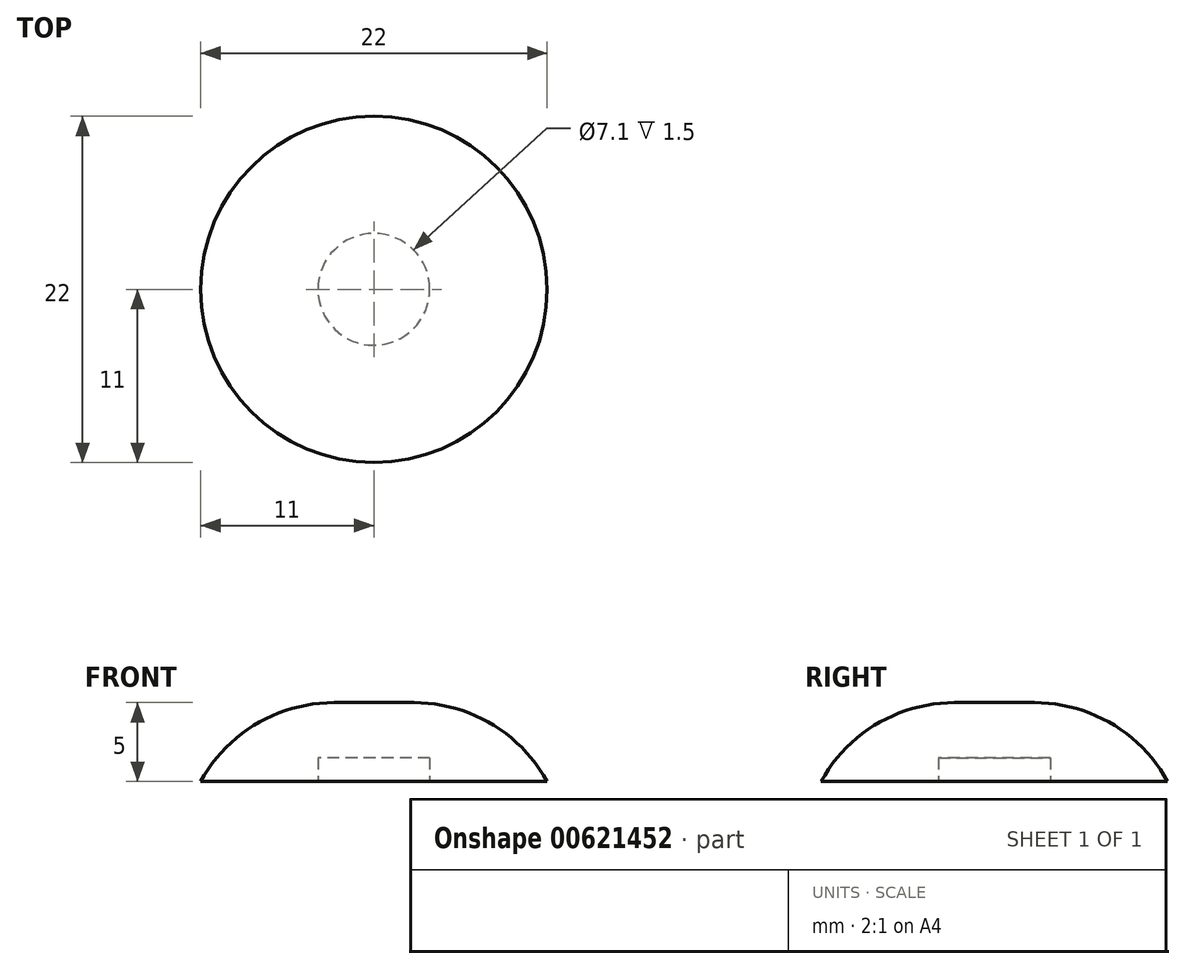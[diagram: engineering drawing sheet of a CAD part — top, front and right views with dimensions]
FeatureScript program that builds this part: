
annotation { "Feature Type Name" : "Feature", "Feature Type Description" : "" }
export const myFeature = defineFeature(function(context is Context, id is Id, definition is map)
    precondition{}
    {
        {
            var Q0;
            Q0=qCreatedBy(makeId("Top.planeOp"),FACE);
            var sketch = newSketch(context, id + "F0", { "sketchPlane" : qUnion([Q0])});
            skCircle(sketch, "E0", {"center": v(0, 0) * mm, "radius": 11 * mm});
            skSolve(sketch);
        }
        {
            var Q0;
            Q0=makeQuery(id+"F0.imprint","IMPRINT",FACE,{"disambiguationData":[TD([[makeQuery(id+"F0.imprint","IMPRINT",EDGE,{"derivedFrom":sQuery(id+"F0.wireOp",EDGE,"E0")}),1.0]])]});
            extrude(context, id + "F1", {"entities" : qUnion([Q0]), "depth" : 5 * mm, "offsetDistance" : 25 * mm});
        }
        {
            var Q0;
            Q0=makeQuery(id+"F1.opExtrude","CAP_EDGE",EDGE,{"disambiguationData":[OSD([sQuery(id+"F0.wireOp",EDGE,"E0")])],"isStart":false});
            fillet(context, id + "F2", {"entities" : qUnion([Q0]), "radius" : 9.66 * mm, "tangentPropagation" : true, "allowEdgeOverflow" : false});
        }
        {
            var Q0;
            Q0=qCreatedBy(makeId("Top.planeOp"),FACE);
            var sketch = newSketch(context, id + "F3", { "sketchPlane" : qUnion([Q0])});
            skCircle(sketch, "E1", {"center": v(0, 0) * mm, "radius": 3.55 * mm});
            skSolve(sketch);
        }
        {
            var Q0;
            Q0=makeQuery(id+"F3.imprint","IMPRINT",FACE,{"disambiguationData":[TD([[makeQuery(id+"F3.imprint","IMPRINT",EDGE,{"derivedFrom":sQuery(id+"F3.wireOp",EDGE,"E1")}),1.0]])]});
            extrude(context, id + "F4", {"entities" : qUnion([Q0]), "operationType" : NewBodyOperationType.REMOVE, "depth" : 1.5 * mm, "offsetDistance" : 25 * mm});
        }
    });
